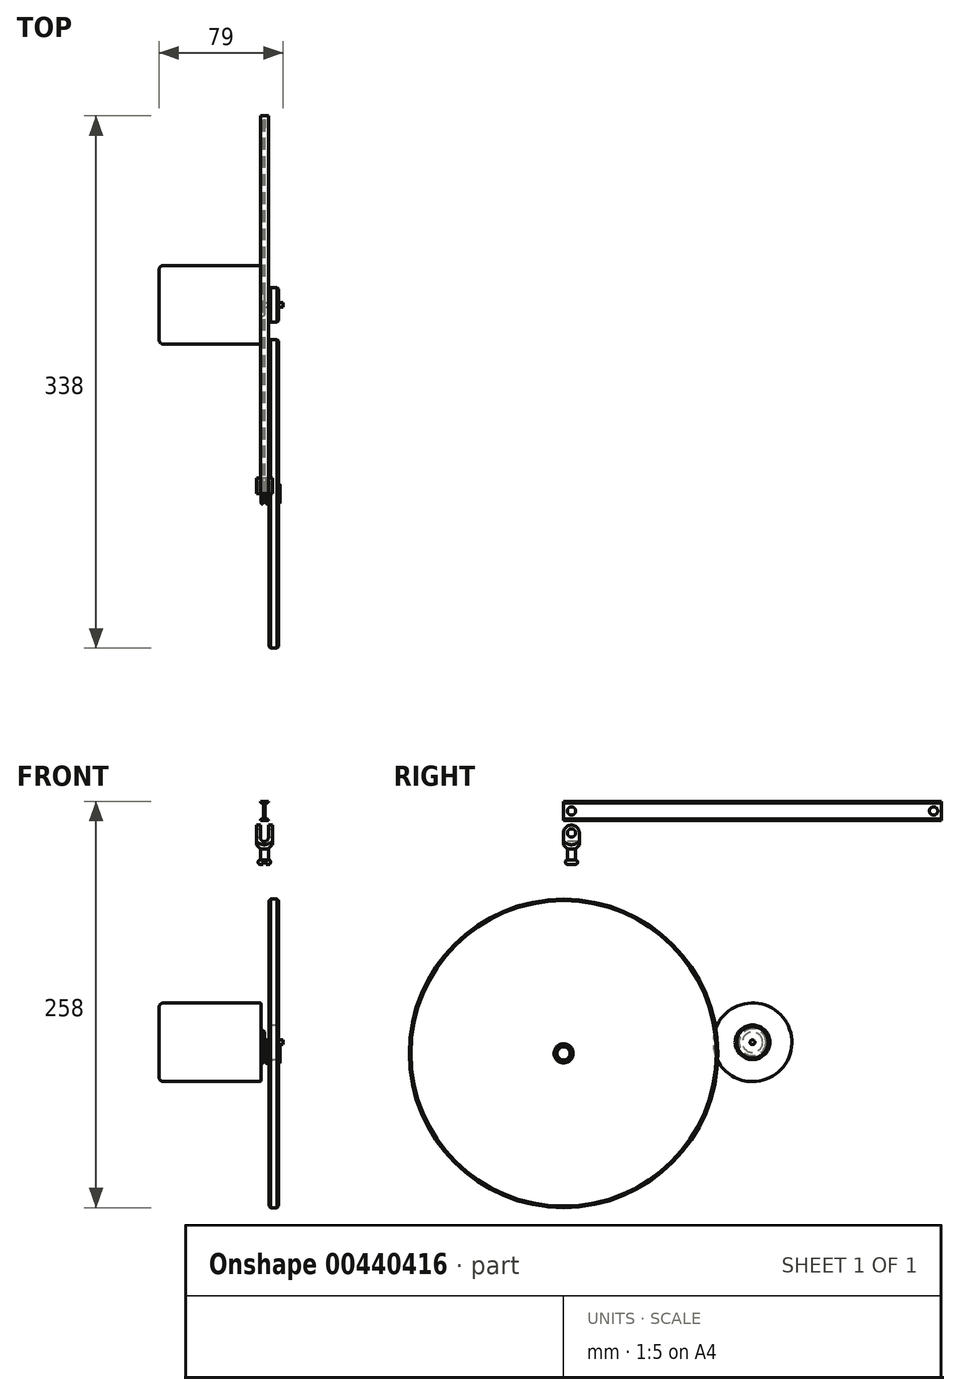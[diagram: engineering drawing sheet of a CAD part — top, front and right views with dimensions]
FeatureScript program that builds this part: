
annotation { "Feature Type Name" : "Feature", "Feature Type Description" : "" }
export const myFeature = defineFeature(function(context is Context, id is Id, definition is map)
    precondition{}
    {
        {
            var Q0;
            Q0=qCreatedBy(makeId("Front.planeOp"),FACE);
            var sketch = newSketch(context, id + "F0", { "sketchPlane" : qUnion([Q0])});
            skLineSegment(sketch, "E0.bottom", {"start": v(-2.5, 6) * mm, "end": v(0, 6) * mm});
            skLineSegment(sketch, "E0.top", {"start": v(-2.5, 0) * mm, "end": v(0, 0) * mm, "construction": true});
            skLineSegment(sketch, "E0.left", {"start": v(-2.5, 6) * mm, "end": v(-2.5, 0) * mm, "construction": true});
            skLineSegment(sketch, "E0.right", {"start": v(0, 6) * mm, "end": v(0, 0) * mm, "construction": true});
            skArc(sketch, "E1", {"start": v(-2.5, 6) * mm, "mid": v(-2.2, 5.3) * mm, "end": v(-1.5, 5) * mm});
            skArc(sketch, "E2", {"start": v(-0.5, 4) * mm, "mid": v(-0.8, 4.7) * mm, "end": v(-1.5, 5) * mm});
            skLineSegment(sketch, "E3", {"start": v(-0.5, 4) * mm, "end": v(-0.5, 0) * mm});
            skLineSegment(sketch, "E4.MirrorCS", {"start": v(0.5, 4) * mm, "end": v(0.5, 0) * mm});
            skLineSegment(sketch, "E5.MirrorCS", {"start": v(2.5, 6) * mm, "end": v(0, 6) * mm});
            skArc(sketch, "E6.MirrorCS", {"start": v(2.5, 6) * mm, "mid": v(2.2, 5.3) * mm, "end": v(1.5, 5) * mm});
            skArc(sketch, "E7.MirrorCS", {"start": v(0.5, 4) * mm, "mid": v(0.8, 4.7) * mm, "end": v(1.5, 5) * mm});
            skArc(sketch, "E8.MirrorCS", {"start": v(-2.5, -6) * mm, "mid": v(-2.2, -5.3) * mm, "end": v(-1.5, -5) * mm});
            skLineSegment(sketch, "E9.MirrorCS", {"start": v(-2.5, -6) * mm, "end": v(0, -6) * mm});
            skLineSegment(sketch, "E10.MirrorCS", {"start": v(2.5, -6) * mm, "end": v(0, -6) * mm});
            skArc(sketch, "E11.MirrorCS", {"start": v(2.5, -6) * mm, "mid": v(2.2, -5.3) * mm, "end": v(1.5, -5) * mm});
            skArc(sketch, "E12.MirrorCS", {"start": v(0.5, -4) * mm, "mid": v(0.8, -4.7) * mm, "end": v(1.5, -5) * mm});
            skArc(sketch, "E13.MirrorCS", {"start": v(-0.5, -4) * mm, "mid": v(-0.8, -4.7) * mm, "end": v(-1.5, -5) * mm});
            skLineSegment(sketch, "E14.MirrorCS", {"start": v(0.5, -4) * mm, "end": v(0.5, 0) * mm});
            skLineSegment(sketch, "E15.MirrorCS", {"start": v(-0.5, -4) * mm, "end": v(-0.5, 0) * mm});
            skSolve(sketch);
        }
        {
            var Q0;
            Q0=makeQuery(id+"F0.imprint","IMPRINT",FACE,{"disambiguationData":[TD([[makeQuery(id+"F0.imprint","IMPRINT",EDGE,{"derivedFrom":sQuery(id+"F0.wireOp",EDGE,"E0.bottom")}),-1.0]])]});
            extrude(context, id + "F1", {"entities" : qUnion([Q0]), "endBound" : BoundingType.SYMMETRIC, "depth" : 240 * mm});
        }
        {
            var Q0;
            Q0=makeQuery(id+"F1.opExtrude","SWEPT_FACE",FACE,{"disambiguationData":[OSD([sQuery(id+"F0.wireOp",EDGE,"E4.MirrorCS"),sQuery(id+"F0.wireOp",EDGE,"E14.MirrorCS")])]});
            var sketch = newSketch(context, id + "F2", { "sketchPlane" : qUnion([Q0])});
            skPoint(sketch, "E16", {"position": v(115, 0) * mm});
            skPoint(sketch, "E17", {"position": v(-115, 0) * mm});
            skSolve(sketch);
        }
        {
            var Q0;
            Q0=sQuery(id+"F2.wireOp",VERTEX,"E16");
            var Q1;
            Q1=sQuery(id+"F2.wireOp",VERTEX,"E17");
            var Q2;
            Q2=makeQuery(id+"F1.opExtrude","SWEPT_BODY",BODY,{"disambiguationData":[OSD([sQuery(id+"F0.wireOp",EDGE,"E0.bottom"),sQuery(id+"F0.wireOp",EDGE,"E1"),sQuery(id+"F0.wireOp",EDGE,"E2"),sQuery(id+"F0.wireOp",EDGE,"E4.MirrorCS"),sQuery(id+"F0.wireOp",EDGE,"E5.MirrorCS"),sQuery(id+"F0.wireOp",EDGE,"E6.MirrorCS"),sQuery(id+"F0.wireOp",EDGE,"E7.MirrorCS"),sQuery(id+"F0.wireOp",EDGE,"E3"),sQuery(id+"F0.wireOp",EDGE,"E8.MirrorCS"),sQuery(id+"F0.wireOp",EDGE,"E9.MirrorCS"),sQuery(id+"F0.wireOp",EDGE,"E10.MirrorCS"),sQuery(id+"F0.wireOp",EDGE,"E11.MirrorCS"),sQuery(id+"F0.wireOp",EDGE,"E12.MirrorCS"),sQuery(id+"F0.wireOp",EDGE,"E13.MirrorCS"),sQuery(id+"F0.wireOp",EDGE,"E14.MirrorCS"),sQuery(id+"F0.wireOp",EDGE,"E15.MirrorCS")])]});
            hole(context, id + "F3", {"style" : HoleStyle.SIMPLE, "endStyle" : HoleEndStyle.THROUGH, "standardTappedOrClearance" : lookupTablePath({ "standard" : "ISO", "fit" : "Close", "size" : "M5", "type" : "Clearance" }), "standardBlindInLast" : lookupTablePath({ "fit" : "Close", "standard" : "ISO", "size" : "M5", "type" : "Clearance" }), "holeDiameter" : 5.25 * mm, "isTappedThrough" : true, "tappedDepth" : 12 * mm, "tapClearance" : 3, "locations" : qUnion([Q0, Q1]), "scope" : qUnion([Q2])});
        }
        {
            var Q0;
            Q0=qCreatedBy(makeId("Right.planeOp"),FACE);
            var sketch = newSketch(context, id + "F4", { "sketchPlane" : qUnion([Q0])});
            skArc(sketch, "E18", {"start": v(-110, -14) * mm, "mid": v(-115, -9) * mm, "end": v(-120, -14) * mm});
            skLineSegment(sketch, "E19", {"start": v(-120, -14) * mm, "end": v(-120, -34) * mm});
            skLineSegment(sketch, "E20", {"start": v(-110, -14) * mm, "end": v(-110, -34) * mm});
            skLineSegment(sketch, "E21", {"start": v(-120, -34) * mm, "end": v(-110, -34) * mm});
            skSolve(sketch);
        }
        {
            var Q0;
            Q0=makeQuery(id+"F4.imprint","IMPRINT",FACE,{"disambiguationData":[TD([[makeQuery(id+"F4.imprint","IMPRINT",EDGE,{"derivedFrom":sQuery(id+"F4.wireOp",EDGE,"E18")}),1.0]])]});
            extrude(context, id + "F5", {"entities" : qUnion([Q0]), "endBound" : BoundingType.SYMMETRIC, "depth" : 10 * mm});
        }
        {
            var Q0;
            Q0=qCreatedBy(makeId("Right.planeOp"),FACE);
            var sketch = newSketch(context, id + "F6", { "sketchPlane" : qUnion([Q0])});
            skLineSegment(sketch, "E22", {"start": v(-117.5, -31) * mm, "end": v(-117.5, -24) * mm});
            skLineSegment(sketch, "E23", {"start": v(-117.5, -24) * mm, "end": v(-124.57, -16.93) * mm});
            skLineSegment(sketch, "E24", {"start": v(-124.57, -16.93) * mm, "end": v(-124.57, -34) * mm});
            skLineSegment(sketch, "E25", {"start": v(-115, -47.77) * mm, "end": v(-115, -34) * mm, "construction": true});
            skArc(sketch, "E26", {"start": v(-117.5, -31) * mm, "mid": v(-119, -32.5) * mm, "end": v(-117.5, -34) * mm});
            skLineSegment(sketch, "E27", {"start": v(-117.5, -34) * mm, "end": v(-124.57, -34) * mm});
            skSolve(sketch);
        }
        {
            var Q0;
            Q0=makeQuery(id+"F6.imprint","IMPRINT",FACE,{"disambiguationData":[TD([[makeQuery(id+"F6.imprint","IMPRINT",EDGE,{"derivedFrom":sQuery(id+"F6.wireOp",EDGE,"E22")}),1.0]])]});
            var Q1;
            Q1=sQuery(id+"F6.wireOp",EDGE,"E25");
            revolve(context, id + "F7", {"operationType" : NewBodyOperationType.REMOVE, "entities" : qUnion([Q0]), "axis" : qUnion([Q1]), "revolveType" : RevolveType.FULL, "oppositeDirection" : true});
        }
        {
            var Q0;
            Q0=makeQuery(id+"F5.opExtrude","CAP_FACE",FACE,{"disambiguationData":[OSD([sQuery(id+"F4.wireOp",EDGE,"E18"),sQuery(id+"F4.wireOp",EDGE,"E19"),sQuery(id+"F4.wireOp",EDGE,"E20"),sQuery(id+"F4.wireOp",EDGE,"E21")])],"isStart":false});
            var sketch = newSketch(context, id + "F8", { "sketchPlane" : qUnion([Q0])});
            skPoint(sketch, "E28", {"position": v(-115, -14) * mm});
            skSolve(sketch);
        }
        {
            var Q0;
            Q0=sQuery(id+"F8.wireOp",VERTEX,"E28");
            var Q1;
            Q1=makeQuery(id+"F5.opExtrude","SWEPT_BODY",BODY,{"disambiguationData":[OSD([sQuery(id+"F4.wireOp",EDGE,"E18"),sQuery(id+"F4.wireOp",EDGE,"E19"),sQuery(id+"F4.wireOp",EDGE,"E20"),sQuery(id+"F4.wireOp",EDGE,"E21")])]});
            hole(context, id + "F9", {"style" : HoleStyle.SIMPLE, "endStyle" : HoleEndStyle.THROUGH, "standardTappedOrClearance" : lookupTablePath({ "standard" : "ISO", "fit" : "Close", "size" : "M5", "type" : "Clearance" }), "standardBlindInLast" : lookupTablePath({ "fit" : "Close", "standard" : "ISO", "size" : "M5", "type" : "Clearance" }), "holeDiameter" : 5.25 * mm, "isTappedThrough" : true, "tappedDepth" : 12 * mm, "tapClearance" : 3, "locations" : qUnion([Q0]), "scope" : qUnion([Q1])});
        }
        {
            var Q0;
            Q0=makeQuery(id+"F5.opExtrude","SWEPT_FACE",FACE,{"disambiguationData":[OSD([sQuery(id+"F4.wireOp",EDGE,"E19")])]});
            var sketch = newSketch(context, id + "F10", { "sketchPlane" : qUnion([Q0])});
            skLineSegment(sketch, "E29", {"start": v(-2.5, -9) * mm, "end": v(-2.5, -17) * mm});
            skLineSegment(sketch, "E30", {"start": v(2.5, -9) * mm, "end": v(2.5, -17) * mm});
            skArc(sketch, "E31", {"start": v(-2.5, -17) * mm, "mid": v(0, -19.5) * mm, "end": v(2.5, -17) * mm});
            skLineSegment(sketch, "E32", {"start": v(-2.5, -9) * mm, "end": v(2.5, -9) * mm});
            skLineSegment(sketch, "E33.bottom", {"start": v(-1, -31) * mm, "end": v(1, -31) * mm});
            skLineSegment(sketch, "E33.top", {"start": v(-1, -34) * mm, "end": v(1, -34) * mm});
            skLineSegment(sketch, "E33.left", {"start": v(-1, -31) * mm, "end": v(-1, -34) * mm});
            skLineSegment(sketch, "E33.right", {"start": v(1, -31) * mm, "end": v(1, -34) * mm});
            skSolve(sketch);
        }
        {
            var Q0;
            {var subQ0=sQuery(id+"F10.wireOp",EDGE,"E31");Q0=makeQuery(id+"F10.imprint","IMPRINT",FACE,{"disambiguationData":[TD([[makeQuery(id+"F10.imprint","IMPRINT",EDGE,{"derivedFrom":subQ0}),1.0]])]});}
            var Q1;
            {var subQ0=sQuery(id+"F10.wireOp",EDGE,"E32");Q1=makeQuery(id+"F10.imprint","IMPRINT",FACE,{"disambiguationData":[TD([[makeQuery(id+"F10.imprint","IMPRINT",EDGE,{"derivedFrom":subQ0}),-1.0]])]});}
            var Q2;
            Q2=makeQuery(id+"F10.imprint","IMPRINT",FACE,{"disambiguationData":[TD([[makeQuery(id+"F10.imprint","IMPRINT",EDGE,{"derivedFrom":sQuery(id+"F10.wireOp",EDGE,"E33.bottom")}),-1.0]])]});
            extrude(context, id + "F11", {"entities" : qUnion([Q0, Q1, Q2]), "operationType" : NewBodyOperationType.REMOVE, "endBound" : BoundingType.THROUGH_ALL, "oppositeDirection" : true, "depth" : 25 * mm});
        }
        {
            var Q0;
            Q0=makeQuery(id+"F1.opExtrude","CAP_FACE",FACE,{"disambiguationData":[OSD([sQuery(id+"F0.wireOp",EDGE,"E0.bottom"),sQuery(id+"F0.wireOp",EDGE,"E1"),sQuery(id+"F0.wireOp",EDGE,"E2"),sQuery(id+"F0.wireOp",EDGE,"E4.MirrorCS"),sQuery(id+"F0.wireOp",EDGE,"E5.MirrorCS"),sQuery(id+"F0.wireOp",EDGE,"E6.MirrorCS"),sQuery(id+"F0.wireOp",EDGE,"E7.MirrorCS"),sQuery(id+"F0.wireOp",EDGE,"E3"),sQuery(id+"F0.wireOp",EDGE,"E8.MirrorCS"),sQuery(id+"F0.wireOp",EDGE,"E9.MirrorCS"),sQuery(id+"F0.wireOp",EDGE,"E10.MirrorCS"),sQuery(id+"F0.wireOp",EDGE,"E11.MirrorCS"),sQuery(id+"F0.wireOp",EDGE,"E12.MirrorCS"),sQuery(id+"F0.wireOp",EDGE,"E13.MirrorCS"),sQuery(id+"F0.wireOp",EDGE,"E14.MirrorCS"),sQuery(id+"F0.wireOp",EDGE,"E15.MirrorCS")])],"isStart":false});
            var sketch = newSketch(context, id + "F12", { "sketchPlane" : qUnion([Q0])});
            skArc(sketch, "E34", {"start": v(-1, -148) * mm, "mid": v(0, -149) * mm, "end": v(1, -148) * mm});
            skArc(sketch, "E35", {"start": v(-1, -148) * mm, "mid": v(-1.5, -147.5) * mm, "end": v(-2, -148) * mm});
            skArc(sketch, "E36", {"start": v(1.5, -147.5) * mm, "mid": v(1.15, -147.65) * mm, "end": v(1, -148) * mm});
            skLineSegment(sketch, "E37", {"start": v(1.5, -147.5) * mm, "end": v(2.5, -147.5) * mm});
            skLineSegment(sketch, "E38", {"start": v(-2, -148) * mm, "end": v(-2, -154) * mm});
            skLineSegment(sketch, "E39", {"start": v(-2, -154) * mm, "end": v(22.27, -154) * mm, "construction": true});
            skArc(sketch, "E40", {"start": v(2.5, -147.5) * mm, "mid": v(2.85, -147.35) * mm, "end": v(3, -147) * mm});
            skLineSegment(sketch, "E41", {"start": v(3, -147) * mm, "end": v(3, -57) * mm});
            skLineSegment(sketch, "E42", {"start": v(3, -57) * mm, "end": v(4, -56) * mm});
            skLineSegment(sketch, "E43", {"start": v(4, -56) * mm, "end": v(8, -56) * mm});
            skLineSegment(sketch, "E44", {"start": v(8, -56) * mm, "end": v(9, -57) * mm});
            skLineSegment(sketch, "E45", {"start": v(9, -57) * mm, "end": v(9, -147.5) * mm});
            skArc(sketch, "E46", {"start": v(9, -147.5) * mm, "mid": v(9.15, -147.85) * mm, "end": v(9.5, -148) * mm});
            skArc(sketch, "E47", {"start": v(10, -148.5) * mm, "mid": v(9.85, -148.15) * mm, "end": v(9.5, -148) * mm});
            skLineSegment(sketch, "E48", {"start": v(10, -148.5) * mm, "end": v(10, -154) * mm});
            skLineSegment(sketch, "E49", {"start": v(-2, -154) * mm, "end": v(10, -154) * mm});
            skSolve(sketch);
        }
        {
            var Q0;
            Q0=makeQuery(id+"F12.imprint","IMPRINT",FACE,{"disambiguationData":[TD([[makeQuery(id+"F12.imprint","IMPRINT",EDGE,{"derivedFrom":sQuery(id+"F12.wireOp",EDGE,"E34")}),-1.0]])]});
            var Q1;
            Q1=sQuery(id+"F12.wireOp",EDGE,"E39");
            revolve(context, id + "F13", {"entities" : qUnion([Q0]), "axis" : qUnion([Q1]), "revolveType" : RevolveType.FULL});
        }
        {
            var Q0;
            Q0=makeQuery(id+"F13.opRevolve","SWEPT_FACE",FACE,{"disambiguationData":[OSD([sQuery(id+"F12.wireOp",EDGE,"E48")])]});
            var sketch = newSketch(context, id + "F14", { "sketchPlane" : qUnion([Q0])});
            skPoint(sketch, "E50", {"position": v(-120, -154) * mm});
            skSolve(sketch);
        }
        {
            var Q0;
            Q0=sQuery(id+"F14.wireOp",VERTEX,"E50");
            var Q1;
            Q1=makeQuery(id+"F13.opRevolve","SWEPT_BODY",BODY,{"disambiguationData":[OSD([sQuery(id+"F12.wireOp",EDGE,"E34"),sQuery(id+"F12.wireOp",EDGE,"E35"),sQuery(id+"F12.wireOp",EDGE,"E36"),sQuery(id+"F12.wireOp",EDGE,"E37"),sQuery(id+"F12.wireOp",EDGE,"E38"),sQuery(id+"F12.wireOp",EDGE,"E40"),sQuery(id+"F12.wireOp",EDGE,"E41"),sQuery(id+"F12.wireOp",EDGE,"E42"),sQuery(id+"F12.wireOp",EDGE,"E43"),sQuery(id+"F12.wireOp",EDGE,"E44"),sQuery(id+"F12.wireOp",EDGE,"E45"),sQuery(id+"F12.wireOp",EDGE,"E46"),sQuery(id+"F12.wireOp",EDGE,"E47"),sQuery(id+"F12.wireOp",EDGE,"E48"),sQuery(id+"F12.wireOp",EDGE,"E49")])]});
            hole(context, id + "F15", {"style" : HoleStyle.SIMPLE, "endStyle" : HoleEndStyle.THROUGH, "standardTappedOrClearance" : lookupTablePath({ "standard" : "ISO", "fit" : "Close", "size" : "M8", "type" : "Clearance" }), "standardBlindInLast" : lookupTablePath({ "fit" : "Close", "standard" : "ISO", "size" : "M8", "type" : "Clearance" }), "holeDiameter" : 8.4 * mm, "isTappedThrough" : true, "tappedDepth" : 12 * mm, "tapClearance" : 3, "locations" : qUnion([Q0]), "scope" : qUnion([Q1])});
        }
        {
            var Q0;
            Q0=qCreatedBy(makeId("Front.planeOp"),FACE);
            var sketch = newSketch(context, id + "F16", { "sketchPlane" : qUnion([Q0])});
            skLineSegment(sketch, "E51.bottom", {"start": v(-64, -121.94) * mm, "end": v(-3, -121.94) * mm});
            skLineSegment(sketch, "E51.top", {"start": v(-67, -146.94) * mm, "end": v(-2, -146.94) * mm});
            skLineSegment(sketch, "E51.left", {"start": v(-67, -124.94) * mm, "end": v(-67, -146.94) * mm});
            skLineSegment(sketch, "E51.right", {"start": v(-2, -122.94) * mm, "end": v(-2, -138.44) * mm});
            skLineSegment(sketch, "E52.bottom", {"start": v(0, -145.44) * mm, "end": v(3, -145.44) * mm});
            skLineSegment(sketch, "E52.top", {"start": v(-3.97, -146.94) * mm, "end": v(12, -146.94) * mm});
            skLineSegment(sketch, "E52.right", {"start": v(12, -145.44) * mm, "end": v(12, -146.94) * mm});
            skLineSegment(sketch, "E53", {"start": v(3, -145.44) * mm, "end": v(3, -136.94) * mm});
            skLineSegment(sketch, "E54", {"start": v(3, -136.94) * mm, "end": v(4, -135.94) * mm});
            skLineSegment(sketch, "E55", {"start": v(4, -135.94) * mm, "end": v(8, -135.94) * mm});
            skLineSegment(sketch, "E56", {"start": v(8, -135.94) * mm, "end": v(9, -136.94) * mm});
            skLineSegment(sketch, "E57", {"start": v(9, -136.94) * mm, "end": v(9, -145.44) * mm});
            skLineSegment(sketch, "E58", {"start": v(-2, -138.44) * mm, "end": v(0, -140.44) * mm});
            skLineSegment(sketch, "E59", {"start": v(0, -140.44) * mm, "end": v(0, -145.44) * mm});
            skLineSegment(sketch, "E60.trimOffspring", {"start": v(9, -145.44) * mm, "end": v(12, -145.44) * mm});
            skPoint(sketch, "E61.visualSharp", {"position": v(-2, -121.94) * mm});
            skArc(sketch, "E61.filletArc", {"start": v(-2, -122.94) * mm, "mid": v(-2.3, -122.23) * mm, "end": v(-3, -121.94) * mm});
            skPoint(sketch, "E62.visualSharp", {"position": v(-67, -121.94) * mm});
            skArc(sketch, "E62.filletArc", {"start": v(-64, -121.94) * mm, "mid": v(-66.12, -122.82) * mm, "end": v(-67, -124.94) * mm});
            skLineSegment(sketch, "E63", {"start": v(-67, -146.94) * mm, "end": v(-110.42, -146.94) * mm, "construction": true});
            skSolve(sketch);
        }
        {
            var Q0;
            Q0=makeQuery(id+"F16.imprint","IMPRINT",FACE,{"disambiguationData":[TD([[makeQuery(id+"F16.imprint","IMPRINT",EDGE,{"derivedFrom":sQuery(id+"F16.wireOp",EDGE,"E51.bottom")}),-1.0]])]});
            var Q1;
            Q1=sQuery(id+"F16.wireOp",EDGE,"E63");
            revolve(context, id + "F17", {"entities" : qUnion([Q0]), "axis" : qUnion([Q1]), "revolveType" : RevolveType.FULL});
        }
    });
